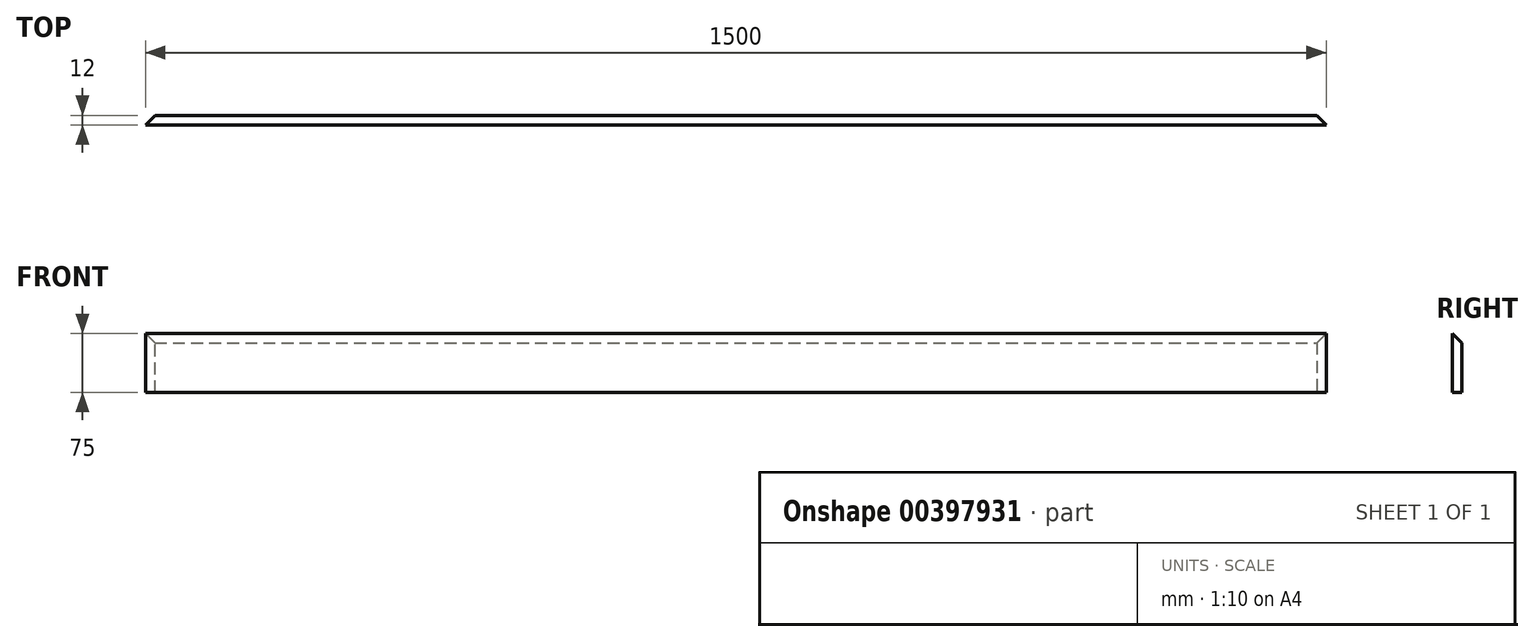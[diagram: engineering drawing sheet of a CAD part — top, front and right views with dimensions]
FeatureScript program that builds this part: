
annotation { "Feature Type Name" : "Feature", "Feature Type Description" : "" }
export const myFeature = defineFeature(function(context is Context, id is Id, definition is map)
    precondition{}
    {
        {
            var Q0;
            Q0=qCreatedBy(makeId("Front.planeOp"),FACE);
            var sketch = newSketch(context, id + "F0", { "sketchPlane" : qUnion([Q0])});
            skLineSegment(sketch, "E0.bottom", {"start": v(750, -37.5) * mm, "end": v(-750, -37.5) * mm});
            skLineSegment(sketch, "E0.top", {"start": v(750, 37.5) * mm, "end": v(-750, 37.5) * mm});
            skLineSegment(sketch, "E0.left", {"start": v(750, -37.5) * mm, "end": v(750, 37.5) * mm});
            skLineSegment(sketch, "E0.right", {"start": v(-750, -37.5) * mm, "end": v(-750, 37.5) * mm});
            skPoint(sketch, "E0.middle", {"position": v(0, 0) * mm});
            skSolve(sketch);
        }
        {
            var Q0;
            Q0 = qSketchRegion(id + "F0", true);
            extrude(context, id + "F1", {"entities" : qUnion([Q0]), "depth" : 12 * mm});
        }
        {
            var Q0;
            Q0=makeQuery(id+"F1.opExtrude","CAP_EDGE",EDGE,{"disambiguationData":[OSD([sQuery(id+"F0.wireOp",EDGE,"E0.top")])],"isStart":true});
            var Q1;
            Q1=makeQuery(id+"F1.opExtrude","CAP_EDGE",EDGE,{"disambiguationData":[OSD([sQuery(id+"F0.wireOp",EDGE,"E0.left")])],"isStart":true});
            var Q2;
            Q2=makeQuery(id+"F1.opExtrude","CAP_EDGE",EDGE,{"disambiguationData":[OSD([sQuery(id+"F0.wireOp",EDGE,"E0.right")])],"isStart":true});
            chamfer(context, id + "F2", {"entities" : qUnion([Q0, Q1, Q2]), "width" : 12 * mm, "tangentPropagation" : true});
        }
    });
